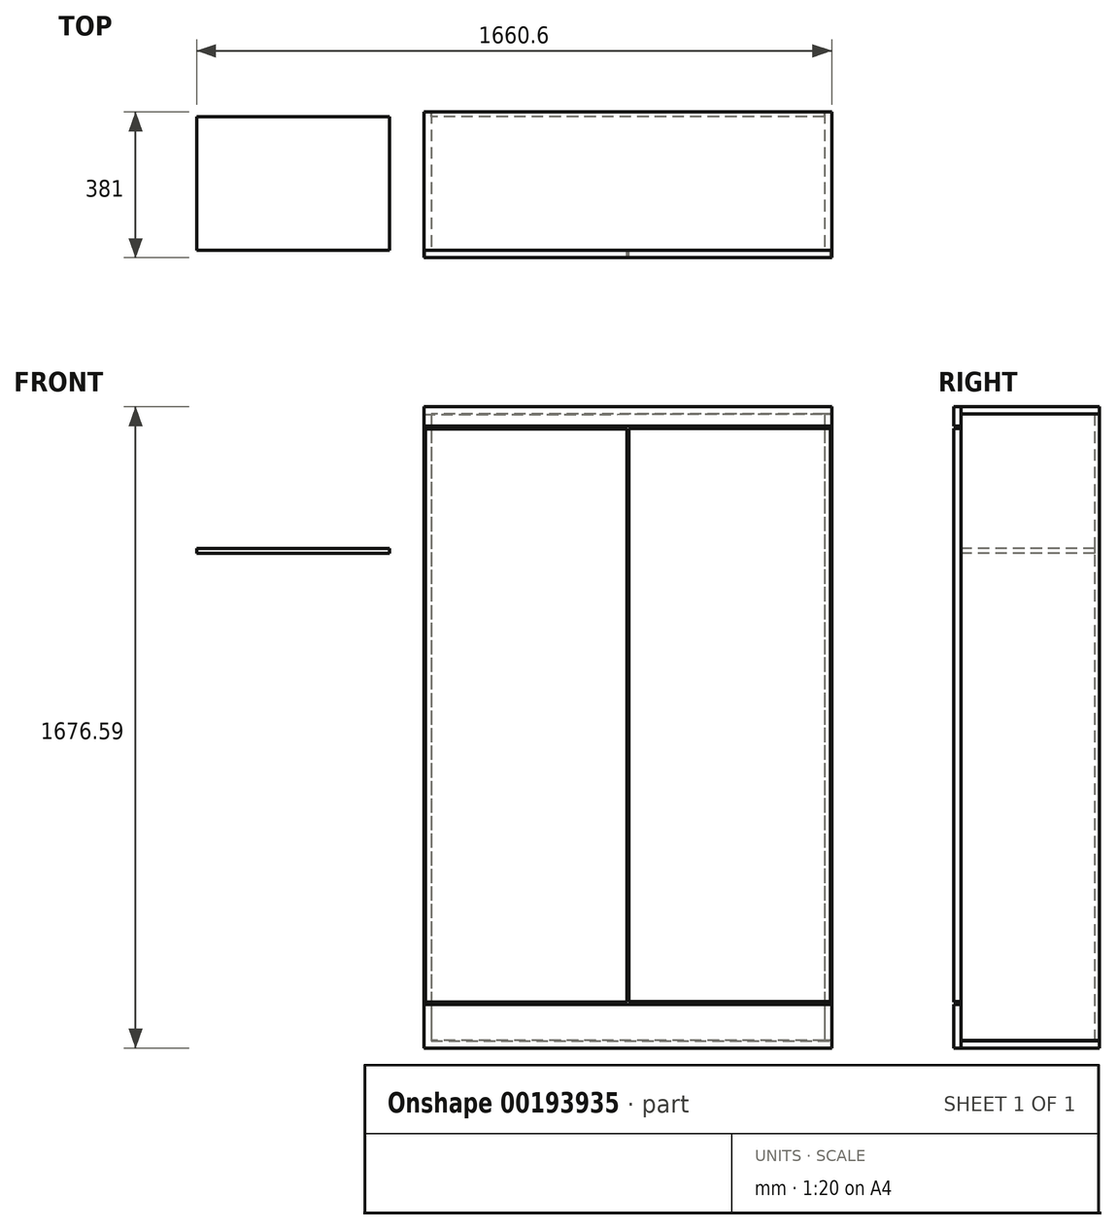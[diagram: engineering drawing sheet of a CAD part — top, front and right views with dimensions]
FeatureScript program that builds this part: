
annotation { "Feature Type Name" : "Feature", "Feature Type Description" : "" }
export const myFeature = defineFeature(function(context is Context, id is Id, definition is map)
    precondition{}
    {
        {
            var Q0;
            Q0=qCreatedBy(makeId("Front.planeOp"),FACE);
            var sketch = newSketch(context, id + "F0", { "sketchPlane" : qUnion([Q0])});
            skLineSegment(sketch, "E0.bottom", {"start": v(-533.94, 45.54) * mm, "end": v(-514.89, 45.54) * mm});
            skLineSegment(sketch, "E0.top", {"start": v(-533.94, -1592.76) * mm, "end": v(-514.89, -1592.76) * mm});
            skLineSegment(sketch, "E0.left", {"start": v(-533.94, 45.54) * mm, "end": v(-533.94, -1592.76) * mm});
            skLineSegment(sketch, "E0.right", {"start": v(-514.89, 45.54) * mm, "end": v(-514.89, -1592.76) * mm});
            skLineSegment(sketch, "E1.bottom", {"start": v(532.86, 45.73) * mm, "end": v(513.81, 45.73) * mm});
            skLineSegment(sketch, "E1.top", {"start": v(532.86, -1592.57) * mm, "end": v(513.81, -1592.57) * mm});
            skLineSegment(sketch, "E1.left", {"start": v(532.86, 45.73) * mm, "end": v(532.86, -1592.57) * mm});
            skLineSegment(sketch, "E1.right", {"start": v(513.81, 45.73) * mm, "end": v(513.81, -1592.57) * mm});
            skLineSegment(sketch, "E2.bottom", {"start": v(-533.94, -1592.76) * mm, "end": v(532.86, -1592.76) * mm});
            skLineSegment(sketch, "E2.top", {"start": v(-533.94, -1611.8) * mm, "end": v(532.86, -1611.8) * mm});
            skLineSegment(sketch, "E2.left", {"start": v(-533.94, -1592.76) * mm, "end": v(-533.94, -1611.8) * mm});
            skLineSegment(sketch, "E2.right", {"start": v(532.86, -1592.76) * mm, "end": v(532.86, -1611.8) * mm});
            skLineSegment(sketch, "E3.top", {"start": v(-501.5, 83.42) * mm, "end": v(-482.46, 83.42) * mm});
            skLineSegment(sketch, "E4.top", {"start": v(565.3, 83.42) * mm, "end": v(546.24, 83.42) * mm});
            skLineSegment(sketch, "E5.bottom", {"start": v(-533.94, 64.6) * mm, "end": v(532.86, 64.78) * mm});
            skLineSegment(sketch, "E5.top", {"start": v(-533.94, 45.54) * mm, "end": v(532.86, 45.73) * mm});
            skLineSegment(sketch, "E5.left", {"start": v(-533.94, 64.6) * mm, "end": v(-533.94, 45.54) * mm});
            skLineSegment(sketch, "E5.right", {"start": v(532.86, 64.78) * mm, "end": v(532.86, 45.73) * mm});
            skLineSegment(sketch, "E6.bottom", {"start": v(-514.89, -1141.9) * mm, "end": v(513.81, -1141.9) * mm});
            skLineSegment(sketch, "E6.top", {"start": v(-514.89, -1160.96) * mm, "end": v(513.81, -1160.96) * mm});
            skLineSegment(sketch, "E6.left", {"start": v(-514.89, -1141.9) * mm, "end": v(-514.89, -1160.96) * mm});
            skLineSegment(sketch, "E6.right", {"start": v(513.81, -1141.9) * mm, "end": v(513.81, -1160.96) * mm});
            skLineSegment(sketch, "E7.bottom", {"start": v(-0.54, -1141.9) * mm, "end": v(8.99, -1141.9) * mm});
            skLineSegment(sketch, "E7.top", {"start": v(-10.06, 45.64) * mm, "end": v(8.99, 45.64) * mm});
            skLineSegment(sketch, "E7.left", {"start": v(-10.06, -1141.9) * mm, "end": v(-10.06, 45.64) * mm});
            skLineSegment(sketch, "E7.right", {"start": v(8.99, -1141.9) * mm, "end": v(8.99, 45.64) * mm});
            skSolve(sketch);
        }
        {
            var Q0;
            {var subQ1=sQuery(id+"F0.wireOp",EDGE,"E1.top");Q0=makeQuery(id+"F0.imprint","IMPRINT",FACE,{"disambiguationData":[TD([[makeQuery(id+"F0.imprint","IMPRINT",EDGE,{"derivedFrom":subQ1}),-1.0]])]});}
            var Q1;
            {var subQ4=sQuery(id+"F0.wireOp",EDGE,"E0.top");Q1=makeQuery(id+"F0.imprint","IMPRINT",FACE,{"disambiguationData":[TD([[makeQuery(id+"F0.imprint","IMPRINT",EDGE,{"derivedFrom":subQ4}),-1.0]])]});}
            var Q2;
            {var subQ4=sQuery(id+"F0.wireOp",EDGE,"E0.bottom");Q2=makeQuery(id+"F0.imprint","IMPRINT",FACE,{"disambiguationData":[TD([[makeQuery(id+"F0.imprint","IMPRINT",EDGE,{"derivedFrom":subQ4}),-1.0]])]});}
            var Q3;
            {var subQ3=sQuery(id+"F0.wireOp",EDGE,"E1.bottom");Q3=makeQuery(id+"F0.imprint","IMPRINT",FACE,{"disambiguationData":[TD([[makeQuery(id+"F0.imprint","IMPRINT",EDGE,{"derivedFrom":subQ3}),-1.0]])]});}
            var Q4;
            Q4=makeQuery(id+"F0.imprint","IMPRINT",FACE,{"disambiguationData":[TD([[makeQuery(id+"F0.imprint","IMPRINT",EDGE,{"derivedFrom":sQuery(id+"F0.wireOp",EDGE,"E2.top")}),1.0]])]});
            extrude(context, id + "F1", {"entities" : qUnion([Q0, Q1, Q2, Q3, Q4]), "oppositeDirection" : true, "depth" : 361.95 * mm});
        }
        {
            var Q0;
            Q0=qCreatedBy(makeId("Right.planeOp"),FACE);
            var sketch = newSketch(context, id + "F2", { "sketchPlane" : qUnion([Q0])});
            skLineSegment(sketch, "E8.bottom", {"start": v(349.25, 46.04) * mm, "end": v(361.95, 46.04) * mm});
            skLineSegment(sketch, "E8.top", {"start": v(349.25, -1592.26) * mm, "end": v(361.95, -1592.26) * mm});
            skLineSegment(sketch, "E8.left", {"start": v(349.25, 46.04) * mm, "end": v(349.25, -1592.26) * mm});
            skLineSegment(sketch, "E8.right", {"start": v(361.95, 46.04) * mm, "end": v(361.95, -1592.26) * mm});
            skSolve(sketch);
        }
        {
            var Q0;
            Q0 = qSketchRegion(id + "F2", true);
            extrude(context, id + "F3", {"entities" : qUnion([Q0]), "endBound" : BoundingType.SYMMETRIC, "depth" : 1028.7 * mm});
        }
        {
            var Q0;
            Q0=makeQuery(id+"F1.opExtrude","SWEPT_FACE",FACE,{"disambiguationData":[OSD([sQuery(id+"F0.wireOp",EDGE,"E1.left")])]});
            var sketch = newSketch(context, id + "F4", { "sketchPlane" : qUnion([Q0])});
            skLineSegment(sketch, "E9.bottom", {"start": v(0, 64.78) * mm, "end": v(-19.05, 64.78) * mm});
            skLineSegment(sketch, "E9.top", {"start": v(0, 13.98) * mm, "end": v(-19.05, 13.98) * mm});
            skLineSegment(sketch, "E9.left", {"start": v(0, 64.78) * mm, "end": v(0, 13.98) * mm});
            skLineSegment(sketch, "E9.right", {"start": v(-19.05, 64.78) * mm, "end": v(-19.05, 13.98) * mm});
            skLineSegment(sketch, "E10.bottom", {"start": v(0, -1611.8) * mm, "end": v(-19.05, -1611.8) * mm});
            skLineSegment(sketch, "E10.top", {"start": v(0, -1497.5) * mm, "end": v(-19.05, -1497.5) * mm});
            skLineSegment(sketch, "E10.left", {"start": v(0, -1611.8) * mm, "end": v(0, -1497.5) * mm});
            skLineSegment(sketch, "E10.right", {"start": v(-19.05, -1611.8) * mm, "end": v(-19.05, -1497.5) * mm});
            skSolve(sketch);
        }
        {
            var Q0;
            Q0 = qSketchRegion(id + "F4", true);
            extrude(context, id + "F5", {"entities" : qUnion([Q0]), "oppositeDirection" : true, "depth" : 1066.8 * mm});
        }
        {
            var Q0;
            Q0=makeQuery(id+"F1.opExtrude","CAP_FACE",FACE,{"disambiguationData":[OSD([sQuery(id+"F0.wireOp",EDGE,"E0.bottom"),sQuery(id+"F0.wireOp",EDGE,"E0.left"),sQuery(id+"F0.wireOp",EDGE,"E0.right"),sQuery(id+"F0.wireOp",EDGE,"E2.bottom"),sQuery(id+"F0.wireOp",EDGE,"E6.left")])],"isStart":true});
            var sketch = newSketch(context, id + "F6", { "sketchPlane" : qUnion([Q0])});
            skLineSegment(sketch, "E11.bottom", {"start": v(-529.62, -1492.08) * mm, "end": v(-2.57, -1492.08) * mm});
            skLineSegment(sketch, "E11.top", {"start": v(-529.62, 6.52) * mm, "end": v(-2.57, 6.52) * mm});
            skLineSegment(sketch, "E11.left", {"start": v(-529.62, -1492.08) * mm, "end": v(-529.62, 6.52) * mm});
            skLineSegment(sketch, "E11.right", {"start": v(-2.57, -1492.08) * mm, "end": v(-2.57, 6.52) * mm});
            skLineSegment(sketch, "E12.bottom", {"start": v(3.08, -1490.99) * mm, "end": v(530.13, -1490.99) * mm});
            skLineSegment(sketch, "E12.top", {"start": v(3.08, 7.61) * mm, "end": v(530.13, 7.61) * mm});
            skLineSegment(sketch, "E12.left", {"start": v(3.08, -1490.99) * mm, "end": v(3.08, 7.61) * mm});
            skLineSegment(sketch, "E12.right", {"start": v(530.13, -1490.99) * mm, "end": v(530.13, 7.61) * mm});
            skSolve(sketch);
        }
        {
            var Q0;
            Q0 = qSketchRegion(id + "F6", true);
            extrude(context, id + "F7", {"entities" : qUnion([Q0]), "depth" : 19.05 * mm});
        }
        {
            var Q0;
            Q0=qCreatedBy(makeId("Front.planeOp"),FACE);
            var sketch = newSketch(context, id + "F8", { "sketchPlane" : qUnion([Q0])});
            skLineSegment(sketch, "E13.bottom", {"start": v(-1127.74, -305.4) * mm, "end": v(-622.92, -305.4) * mm});
            skLineSegment(sketch, "E13.top", {"start": v(-1127.74, -318.1) * mm, "end": v(-622.92, -318.1) * mm});
            skLineSegment(sketch, "E13.left", {"start": v(-1127.74, -305.4) * mm, "end": v(-1127.74, -318.1) * mm});
            skLineSegment(sketch, "E13.right", {"start": v(-622.92, -305.4) * mm, "end": v(-622.92, -318.1) * mm});
            skSolve(sketch);
        }
        {
            var Q0;
            Q0=makeQuery(id+"F8.imprint","IMPRINT",FACE,{"disambiguationData":[TD([[makeQuery(id+"F8.imprint","IMPRINT",EDGE,{"derivedFrom":sQuery(id+"F8.wireOp",EDGE,"E13.bottom")}),-1.0]])]});
            extrude(context, id + "F9", {"entities" : qUnion([Q0]), "oppositeDirection" : true, "depth" : 349.25 * mm});
        }
    });
